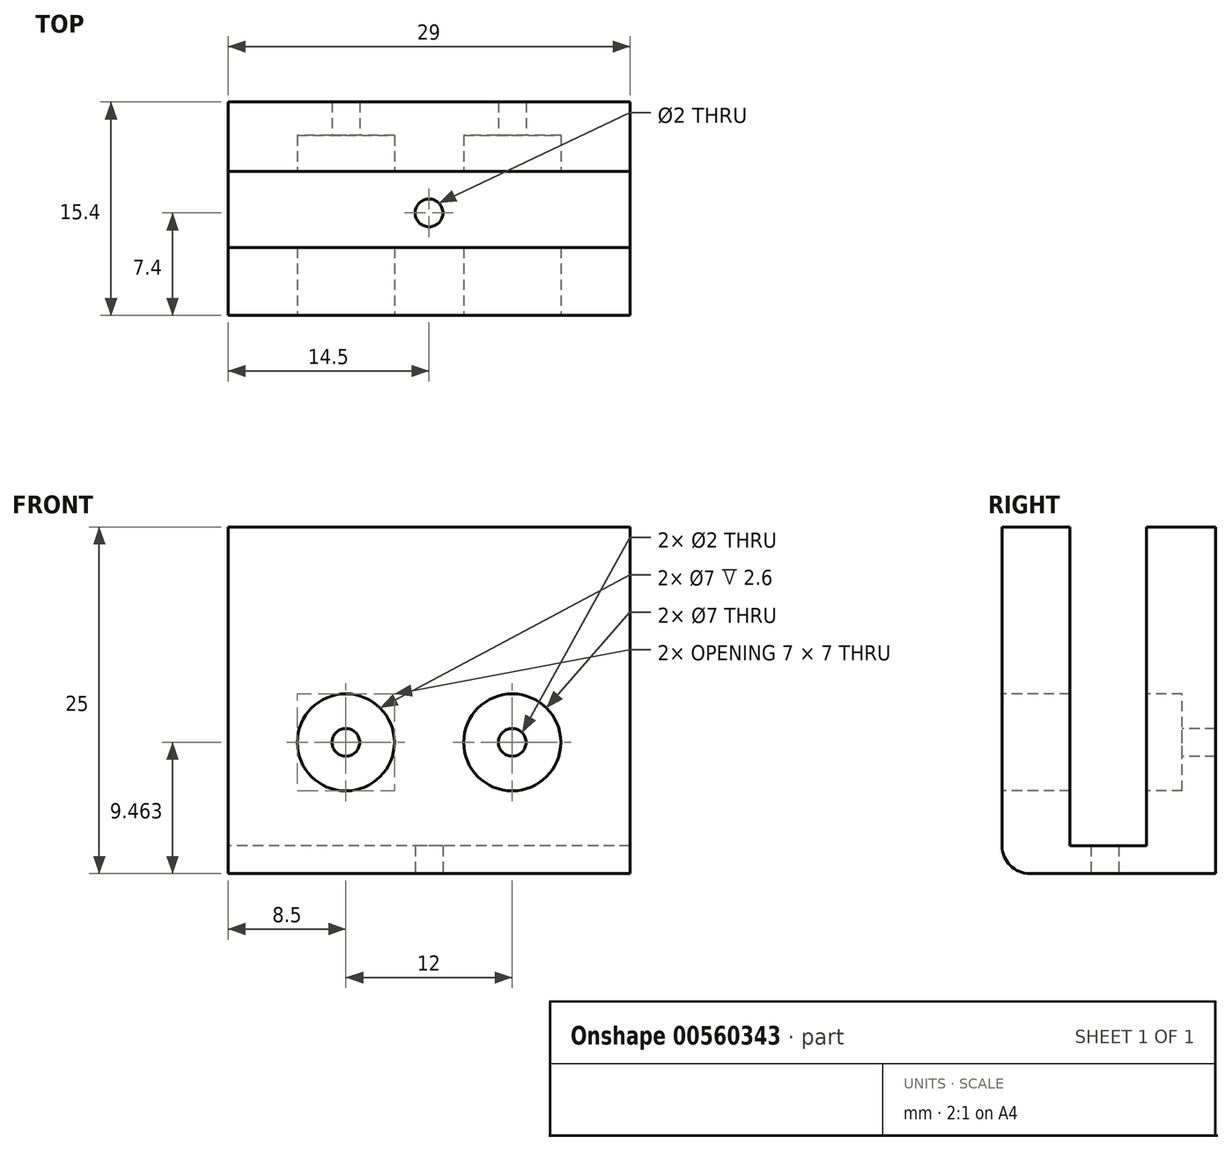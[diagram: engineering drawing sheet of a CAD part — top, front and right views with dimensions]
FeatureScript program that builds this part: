
annotation { "Feature Type Name" : "Feature", "Feature Type Description" : "" }
export const myFeature = defineFeature(function(context is Context, id is Id, definition is map)
    precondition{}
    {
        {
            var Q0;
            Q0=qCreatedBy(makeId("Top.planeOp"),FACE);
            var sketch = newSketch(context, id + "F0", { "sketchPlane" : qUnion([Q0])});
            skLineSegment(sketch, "E0", {"start": v(-14.5, 0) * mm, "end": v(-14.5, -5.5) * mm});
            skLineSegment(sketch, "E1", {"start": v(-14.5, -5.5) * mm, "end": v(14.5, -5.5) * mm});
            skLineSegment(sketch, "E2", {"start": v(14.5, -5.5) * mm, "end": v(14.5, 0) * mm});
            skLineSegment(sketch, "E3", {"start": v(-14.5, -5.5) * mm, "end": v(-14.5, -10.4) * mm});
            skLineSegment(sketch, "E4", {"start": v(-14.5, -10.4) * mm, "end": v(14.5, -10.4) * mm});
            skLineSegment(sketch, "E5", {"start": v(14.5, -10.4) * mm, "end": v(14.5, -5.5) * mm});
            skCircle(sketch, "E6", {"center": v(0, -3) * mm, "radius": 1 * mm});
            skLineSegment(sketch, "E7", {"start": v(-14.5, 0) * mm, "end": v(14.5, 0) * mm});
            skLineSegment(sketch, "E8", {"start": v(-14.5, 0) * mm, "end": v(-14.5, 5) * mm});
            skLineSegment(sketch, "E9", {"start": v(-14.5, 5) * mm, "end": v(14.5, 5) * mm});
            skLineSegment(sketch, "E10", {"start": v(14.5, 5) * mm, "end": v(14.5, 0) * mm});
            skSolve(sketch);
        }
        {
            var Q0;
            Q0=makeQuery(id+"F0.imprint","IMPRINT",FACE,{"disambiguationData":[TD([[makeQuery(id+"F0.imprint","IMPRINT",EDGE,{"derivedFrom":sQuery(id+"F0.wireOp",EDGE,"E1")}),-1.0]])]});
            var Q1;
            Q1=makeQuery(id+"F0.imprint","IMPRINT",FACE,{"disambiguationData":[TD([[makeQuery(id+"F0.imprint","IMPRINT",EDGE,{"derivedFrom":sQuery(id+"F0.wireOp",EDGE,"E0")}),1.0]])]});
            var Q2;
            Q2=makeQuery(id+"F0.imprint","IMPRINT",FACE,{"disambiguationData":[TD([[makeQuery(id+"F0.imprint","IMPRINT",EDGE,{"derivedFrom":sQuery(id+"F0.wireOp",EDGE,"E7")}),1.0]])]});
            extrude(context, id + "F1", {"entities" : qUnion([Q0, Q1, Q2]), "depth" : 2 * mm});
        }
        {
            var Q0;
            Q0=makeQuery(id+"F0.imprint","IMPRINT",FACE,{"disambiguationData":[TD([[makeQuery(id+"F0.imprint","IMPRINT",EDGE,{"derivedFrom":sQuery(id+"F0.wireOp",EDGE,"E1")}),-1.0]])]});
            var Q1;
            Q1=makeQuery(id+"F0.imprint","IMPRINT",FACE,{"disambiguationData":[TD([[makeQuery(id+"F0.imprint","IMPRINT",EDGE,{"derivedFrom":sQuery(id+"F0.wireOp",EDGE,"E7")}),1.0]])]});
            extrude(context, id + "F2", {"entities" : qUnion([Q0, Q1]), "operationType" : NewBodyOperationType.ADD, "depth" : 25 * mm});
        }
        {
            var Q0;
            {var subQ0=sQuery(id+"F0.wireOp",EDGE,"E4");Q0=makeQuery(id+"F2.boolean.opBoolean","MERGE",FACE,{"derivedFrom":[makeQuery(id+"F1.opExtrude","SWEPT_FACE",FACE,{"disambiguationData":[OSD([subQ0])]}),makeQuery(id+"F2.opExtrude","SWEPT_FACE",FACE,{"disambiguationData":[OSD([subQ0])]})]});}
            var sketch = newSketch(context, id + "F3", { "sketchPlane" : qUnion([Q0])});
            skCircle(sketch, "E11", {"center": v(-6, 9.46) * mm, "radius": 1 * mm});
            skCircle(sketch, "E12", {"center": v(6, 9.46) * mm, "radius": 1 * mm});
            skCircle(sketch, "E13", {"center": v(-6, 9.46) * mm, "radius": 3.5 * mm});
            skCircle(sketch, "E14", {"center": v(6, 9.46) * mm, "radius": 3.5 * mm});
            skSolve(sketch);
        }
        {
            var Q0;
            Q0=makeQuery(id+"F3.imprint","IMPRINT",FACE,{"disambiguationData":[TD([[makeQuery(id+"F3.imprint","IMPRINT",EDGE,{"derivedFrom":sQuery(id+"F3.wireOp",EDGE,"E12")}),1.0]])]});
            var Q1;
            Q1=makeQuery(id+"F3.imprint","IMPRINT",FACE,{"disambiguationData":[TD([[makeQuery(id+"F3.imprint","IMPRINT",EDGE,{"derivedFrom":sQuery(id+"F3.wireOp",EDGE,"E11")}),1.0]])]});
            extrude(context, id + "F4", {"entities" : qUnion([Q0, Q1]), "operationType" : NewBodyOperationType.REMOVE, "oppositeDirection" : true, "depth" : 25 * mm, "offsetDistance" : 25 * mm});
        }
        {
            var Q0;
            Q0=makeQuery(id+"F3.imprint","IMPRINT",FACE,{"disambiguationData":[TD([[makeQuery(id+"F3.imprint","IMPRINT",EDGE,{"derivedFrom":sQuery(id+"F3.wireOp",EDGE,"E11")}),-1.0]])]});
            var Q1;
            Q1=makeQuery(id+"F3.imprint","IMPRINT",FACE,{"disambiguationData":[TD([[makeQuery(id+"F3.imprint","IMPRINT",EDGE,{"derivedFrom":sQuery(id+"F3.wireOp",EDGE,"E12")}),-1.0]])]});
            extrude(context, id + "F5", {"entities" : qUnion([Q0, Q1]), "operationType" : NewBodyOperationType.REMOVE, "oppositeDirection" : true, "depth" : 13 * mm});
        }
        {
            var Q0;
            Q0=makeQuery(id+"F1.opExtrude","CAP_EDGE",EDGE,{"disambiguationData":[OSD([sQuery(id+"F0.wireOp",EDGE,"E4")])],"isStart":true});
            fillet(context, id + "F6", {"entities" : qUnion([Q0]), "radius" : 2 * mm, "tangentPropagation" : true, "allowEdgeOverflow" : false});
        }
    });
